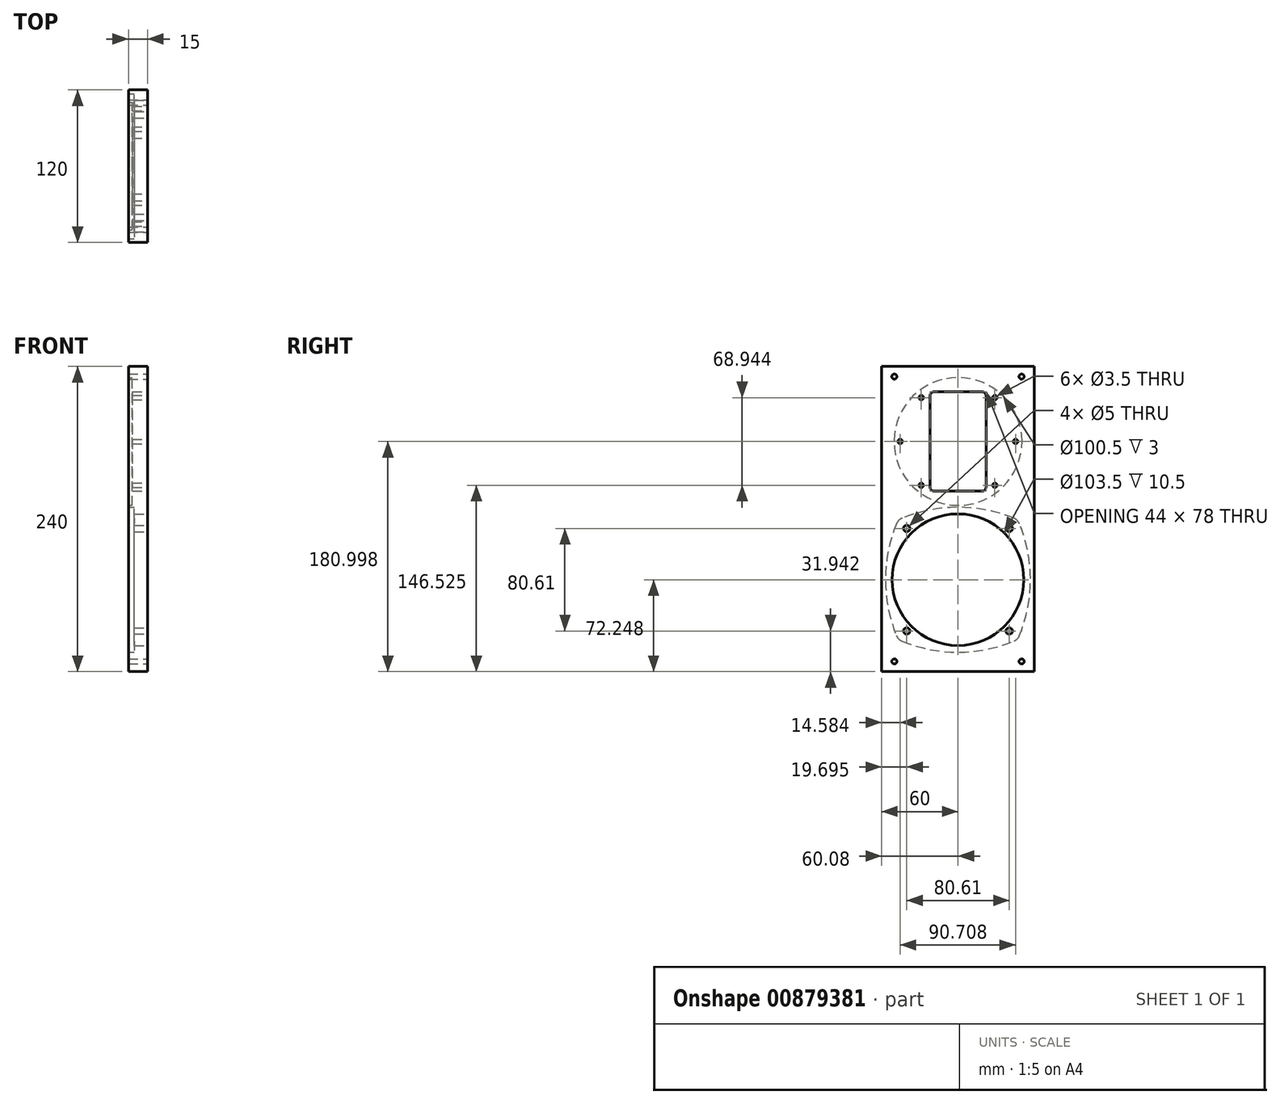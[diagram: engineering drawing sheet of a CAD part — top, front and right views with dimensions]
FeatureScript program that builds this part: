
annotation { "Feature Type Name" : "Feature", "Feature Type Description" : "" }
export const myFeature = defineFeature(function(context is Context, id is Id, definition is map)
    precondition{}
    {
        {
            var Q0;
            Q0=qCreatedBy(makeId("Right.planeOp"),FACE);
            var sketch = newSketch(context, id + "F0", { "sketchPlane" : qUnion([Q0])});
            skLineSegment(sketch, "E0.bottom", {"start": v(60, 118.4) * mm, "end": v(-60, 118.4) * mm});
            skLineSegment(sketch, "E1", {"start": v(60, -121.6) * mm, "end": v(-60, -121.6) * mm});
            skPoint(sketch, "E2", {"position": v(0, -49.34) * mm});
            skCircle(sketch, "E3", {"center": v(0, -49.34) * mm, "radius": 51.75 * mm});
            skCircle(sketch, "E4", {"center": v(40.3, -9.04) * mm, "radius": 2.5 * mm});
            skPoint(sketch, "E5", {"position": v(46.32, -3.03) * mm});
            skPoint(sketch, "E6", {"position": v(47.02, -2.32) * mm});
            skCircle(sketch, "E7.1.0", {"center": v(-40.3, -9.04) * mm, "radius": 2.5 * mm});
            skPoint(sketch, "E7.1.1", {"position": v(-46.32, -3.03) * mm});
            skPoint(sketch, "E7.1.2", {"position": v(-47.02, -2.32) * mm});
            skCircle(sketch, "E7.2.0", {"center": v(-40.3, -89.65) * mm, "radius": 2.5 * mm});
            skPoint(sketch, "E7.2.1", {"position": v(-46.32, -95.66) * mm});
            skPoint(sketch, "E7.2.2", {"position": v(-47.02, -96.37) * mm});
            skCircle(sketch, "E7.3.0", {"center": v(40.3, -89.65) * mm, "radius": 2.5 * mm});
            skPoint(sketch, "E7.3.1", {"position": v(46.32, -95.66) * mm});
            skPoint(sketch, "E7.3.2", {"position": v(47.02, -96.37) * mm});
            skPoint(sketch, "E8.1.0", {"position": v(-57, -49.34) * mm});
            skPoint(sketch, "E8.2.0", {"position": v(0, -106.34) * mm});
            skPoint(sketch, "E8.3.0", {"position": v(57, -49.34) * mm});
            skArc(sketch, "E9", {"start": v(43.97, -1.01) * mm, "mid": v(0, 7.66) * mm, "end": v(-43.97, -1.01) * mm});
            skArc(sketch, "E10", {"start": v(-48.33, -5.38) * mm, "mid": v(-57, -49.34) * mm, "end": v(-48.33, -93.3) * mm});
            skArc(sketch, "E11", {"start": v(-43.97, -97.67) * mm, "mid": v(0, -106.34) * mm, "end": v(43.97, -97.67) * mm});
            skArc(sketch, "E12", {"start": v(48.33, -93.3) * mm, "mid": v(57, -49.34) * mm, "end": v(48.33, -5.38) * mm});
            skPoint(sketch, "E13", {"position": v(29, 93.88) * mm});
            skLineSegment(sketch, "E14", {"start": v(0.08, 59.4) * mm, "end": v(0, 59.4) * mm});
            skLineSegment(sketch, "E15", {"start": v(0, 59.4) * mm, "end": v(0.08, 59.4) * mm});
            skPoint(sketch, "E16.MirrorP", {"position": v(29, 24.94) * mm});
            skCircle(sketch, "E17", {"center": v(29, 93.88) * mm, "radius": 1.75 * mm});
            skCircle(sketch, "E18", {"center": v(-28.85, 93.88) * mm, "radius": 1.75 * mm});
            skCircle(sketch, "E19", {"center": v(29, 24.94) * mm, "radius": 1.75 * mm});
            skCircle(sketch, "E20", {"center": v(-28.85, 24.94) * mm, "radius": 1.75 * mm});
            skPoint(sketch, "E21.orphan", {"position": v(0.08, 59.4) * mm});
            skLineSegment(sketch, "E22.bottom", {"start": v(19.08, 98.4) * mm, "end": v(-18.92, 98.4) * mm});
            skLineSegment(sketch, "E22.top", {"start": v(19.08, 20.4) * mm, "end": v(-18.92, 20.4) * mm});
            skLineSegment(sketch, "E22.left", {"start": v(22.08, 95.4) * mm, "end": v(22.08, 23.4) * mm});
            skLineSegment(sketch, "E22.right", {"start": v(-21.92, 95.4) * mm, "end": v(-21.92, 23.4) * mm});
            skPoint(sketch, "E23.visualSharp", {"position": v(22.08, 98.4) * mm});
            skArc(sketch, "E23.filletArc", {"start": v(22.08, 95.4) * mm, "mid": v(21.2, 97.53) * mm, "end": v(19.08, 98.4) * mm});
            skPoint(sketch, "E24.visualSharp", {"position": v(-21.92, 98.4) * mm});
            skArc(sketch, "E24.filletArc", {"start": v(-18.92, 98.4) * mm, "mid": v(-21.04, 97.53) * mm, "end": v(-21.92, 95.4) * mm});
            skPoint(sketch, "E25.visualSharp", {"position": v(-21.92, 20.4) * mm});
            skArc(sketch, "E25.filletArc", {"start": v(-21.92, 23.4) * mm, "mid": v(-21.04, 21.29) * mm, "end": v(-18.92, 20.4) * mm});
            skPoint(sketch, "E26.visualSharp", {"position": v(22.08, 20.4) * mm});
            skArc(sketch, "E26.filletArc", {"start": v(19.08, 20.4) * mm, "mid": v(21.2, 21.29) * mm, "end": v(22.08, 23.4) * mm});
            skLineSegment(sketch, "E27", {"start": v(60, 118.4) * mm, "end": v(60, -121.6) * mm});
            skLineSegment(sketch, "E28", {"start": v(-60, 118.4) * mm, "end": v(-60, -121.6) * mm});
            skPoint(sketch, "E29.orphan", {"position": v(0, 118.4) * mm});
            skCircle(sketch, "E30", {"center": v(0.08, 59.4) * mm, "radius": 50.25 * mm});
            skLineSegment(sketch, "E31.bottom", {"start": v(-60, 118.4) * mm, "end": v(60, 118.4) * mm});
            skLineSegment(sketch, "E31.top", {"start": v(-60, -121.6) * mm, "end": v(60, -121.6) * mm});
            skPoint(sketch, "E32.trimOffspring.end.orphan", {"position": v(0, -121.6) * mm});
            skCircle(sketch, "E33.0.1.0", {"center": v(-50, 110.4) * mm, "radius": 2 * mm});
            skCircle(sketch, "E34.0.1.0", {"center": v(50, 110.4) * mm, "radius": 2 * mm});
            skCircle(sketch, "E35.0.1.0", {"center": v(50, -113.6) * mm, "radius": 2 * mm});
            skCircle(sketch, "E36.0.1.0", {"center": v(-50, -113.6) * mm, "radius": 2 * mm});
            skPoint(sketch, "E37", {"position": v(0.14, 59.47) * mm});
            skLineSegment(sketch, "E38", {"start": v(0.14, 59.47) * mm, "end": v(0.22, 59.47) * mm});
            skPoint(sketch, "E38.endSnap0", {"position": v(22.14, 59.47) * mm});
            skLineSegment(sketch, "E39", {"start": v(0.14, 59.47) * mm, "end": v(0.22, 59.38) * mm});
            skCircle(sketch, "E40.3.0", {"center": v(45.3, 59.4) * mm, "radius": 1.75 * mm});
            skCircle(sketch, "E41.3.0", {"center": v(-45.42, 59.4) * mm, "radius": 1.75 * mm});
            skPoint(sketch, "E42.trimOffspring.end.orphan", {"position": v(45.14, 59.47) * mm});
            skLineSegment(sketch, "E43.trimOffspring", {"start": v(0.22, 59.38) * mm, "end": v(0.22, 59.47) * mm});
            skArc(sketch, "E44.filletArc", {"start": v(48.33, -5.38) * mm, "mid": v(46.58, -2.76) * mm, "end": v(43.97, -1.01) * mm});
            skArc(sketch, "E45.filletArc", {"start": v(-43.97, -1.01) * mm, "mid": v(-46.58, -2.76) * mm, "end": v(-48.33, -5.38) * mm});
            skArc(sketch, "E46.filletArc", {"start": v(-48.33, -93.3) * mm, "mid": v(-46.58, -95.93) * mm, "end": v(-43.97, -97.67) * mm});
            skArc(sketch, "E47.filletArc", {"start": v(43.97, -97.67) * mm, "mid": v(46.58, -95.93) * mm, "end": v(48.33, -93.3) * mm});
            skLineSegment(sketch, "E48", {"start": v(0, -49.34) * mm, "end": v(-51.15, -100.5) * mm, "construction": true});
            skLineSegment(sketch, "E49", {"start": v(0, -49.34) * mm, "end": v(51.28, 1.9) * mm, "construction": true});
            skSolve(sketch);
        }
        {
            var Q0;
            Q0=makeQuery(id+"F0.imprint","IMPRINT",FACE,{"disambiguationData":[TD([[makeQuery(id+"F0.imprint","IMPRINT",EDGE,{"derivedFrom":sQuery(id+"F0.wireOp",EDGE,"E1")}),-1.0]])]});
            var Q1;
            Q1=makeQuery(id+"F0.imprint","IMPRINT",FACE,{"disambiguationData":[TD([[makeQuery(id+"F0.imprint","IMPRINT",EDGE,{"derivedFrom":sQuery(id+"F0.wireOp",EDGE,"E9")}),-1.0]])]});
            extrude(context, id + "F1", {"entities" : qUnion([Q0, Q1]), "oppositeDirection" : true, "depth" : 15 * mm, "offsetDistance" : 25 * mm});
        }
        {
            var Q0;
            Q0=makeQuery(id+"F0.imprint","IMPRINT",FACE,{"disambiguationData":[TD([[makeQuery(id+"F0.imprint","IMPRINT",EDGE,{"derivedFrom":sQuery(id+"F0.wireOp",EDGE,"E17")}),-1.0]])]});
            extrude(context, id + "F2", {"entities" : qUnion([Q0]), "operationType" : NewBodyOperationType.ADD, "oppositeDirection" : true, "depth" : 12 * mm, "offsetDistance" : 25 * mm});
        }
        {
            var Q0;
            Q0=makeQuery(id+"F0.imprint","IMPRINT",FACE,{"disambiguationData":[TD([[makeQuery(id+"F0.imprint","IMPRINT",EDGE,{"derivedFrom":sQuery(id+"F0.wireOp",EDGE,"E3")}),-1.0]])]});
            extrude(context, id + "F3", {"entities" : qUnion([Q0]), "operationType" : NewBodyOperationType.ADD, "oppositeDirection" : true, "depth" : 10.5 * mm, "offsetDistance" : 25 * mm});
        }
    });
